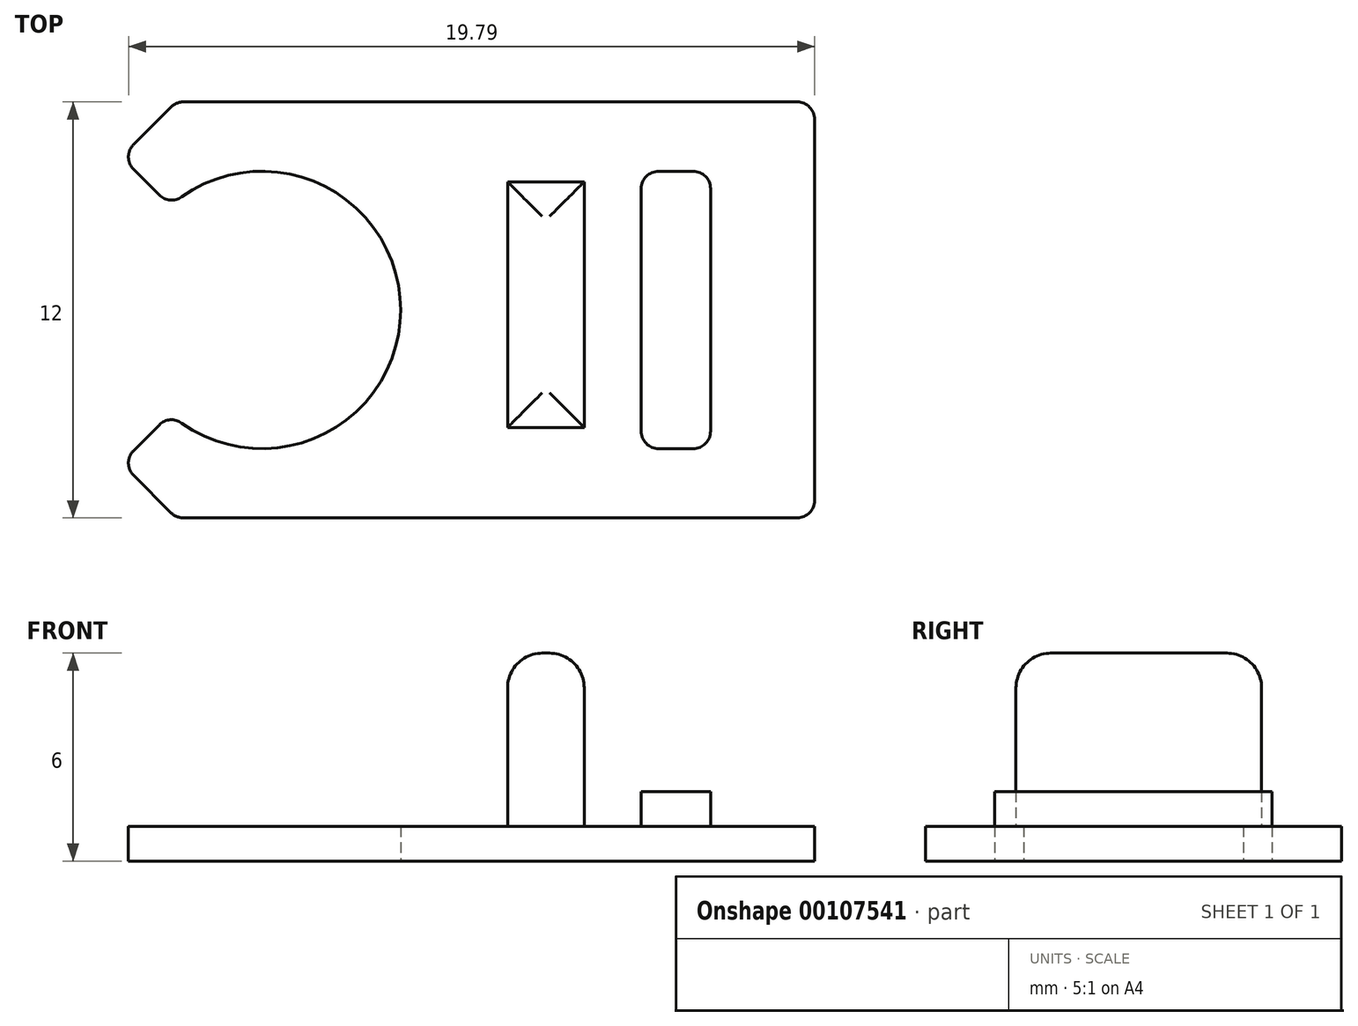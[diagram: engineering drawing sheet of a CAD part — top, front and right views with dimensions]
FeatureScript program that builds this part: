
annotation { "Feature Type Name" : "Feature", "Feature Type Description" : "" }
export const myFeature = defineFeature(function(context is Context, id is Id, definition is map)
    precondition{}
    {
        {
            var Q0;
            Q0=qCreatedBy(makeId("Top.planeOp"),FACE);
            var sketch = newSketch(context, id + "F0", { "sketchPlane" : qUnion([Q0])});
            skArc(sketch, "E0", {"start": v(-2.65, -3) * mm, "mid": v(4, 0) * mm, "end": v(-2.65, 3) * mm});
            skLineSegment(sketch, "E1", {"start": v(-2.65, 3) * mm, "end": v(-4.06, 4.41) * mm});
            skLineSegment(sketch, "E2", {"start": v(-4.06, 4.41) * mm, "end": v(-2.47, 6) * mm});
            skLineSegment(sketch, "E3", {"start": v(-2.47, 6) * mm, "end": v(15.94, 6) * mm});
            skLineSegment(sketch, "E4", {"start": v(15.94, 6) * mm, "end": v(15.94, -6) * mm});
            skLineSegment(sketch, "E5", {"start": v(15.94, -6) * mm, "end": v(-2.47, -6) * mm});
            skLineSegment(sketch, "E6", {"start": v(-2.47, -6) * mm, "end": v(-4.06, -4.41) * mm});
            skLineSegment(sketch, "E7", {"start": v(-4.06, -4.41) * mm, "end": v(-2.65, -3) * mm});
            skLineSegment(sketch, "E8", {"start": v(-2.65, 3) * mm, "end": v(-2.65, -3) * mm, "construction": true});
            skLineSegment(sketch, "E9", {"start": v(0, 0) * mm, "end": v(-2.65, 0) * mm, "construction": true});
            skSolve(sketch);
        }
        {
            var Q0;
            Q0 = qSketchRegion(id + "F0", true);
            extrude(context, id + "F1", {"entities" : qUnion([Q0]), "depth" : 1 * mm});
        }
        {
            var Q0;
            Q0=makeQuery(id+"F1.opExtrude","CAP_FACE",FACE,{"disambiguationData":[OSD([sQuery(id+"F0.wireOp",EDGE,"E0"),sQuery(id+"F0.wireOp",EDGE,"E1"),sQuery(id+"F0.wireOp",EDGE,"E2"),sQuery(id+"F0.wireOp",EDGE,"E3"),sQuery(id+"F0.wireOp",EDGE,"E4"),sQuery(id+"F0.wireOp",EDGE,"E5"),sQuery(id+"F0.wireOp",EDGE,"E6"),sQuery(id+"F0.wireOp",EDGE,"E7")])],"isStart":false});
            var sketch = newSketch(context, id + "F2", { "sketchPlane" : qUnion([Q0])});
            skLineSegment(sketch, "E10.bottom", {"start": v(10.94, 4) * mm, "end": v(12.94, 4) * mm});
            skLineSegment(sketch, "E10.top", {"start": v(10.94, -4) * mm, "end": v(12.94, -4) * mm});
            skLineSegment(sketch, "E10.left", {"start": v(10.94, 4) * mm, "end": v(10.94, -4) * mm});
            skLineSegment(sketch, "E10.right", {"start": v(12.94, 4) * mm, "end": v(12.94, -4) * mm});
            skLineSegment(sketch, "E11", {"start": v(0, 0) * mm, "end": v(10.94, 0) * mm, "construction": true});
            skSolve(sketch);
        }
        {
            var Q0;
            Q0 = qSketchRegion(id + "F2", true);
            extrude(context, id + "F3", {"entities" : qUnion([Q0]), "operationType" : NewBodyOperationType.ADD, "depth" : 1 * mm});
        }
        {
            var Q0;
            Q0=makeQuery(id+"FxF9EGAjR56P1E0_1.boolean.opBoolean","MERGE",EDGE,{"derivedFrom":[makeQuery(id+"F1.opExtrude","SWEPT_EDGE",EDGE,{"disambiguationData":[OSD([sQuery(id+"F0.wireOp",EDGE,"E4"),sQuery(id+"F0.wireOp",EDGE,"E5")])]}),makeQuery(id+"FxF9EGAjR56P1E0_1.opExtrude","SWEPT_EDGE",EDGE,{"disambiguationData":[OSD([sQuery(id+"Fv8JB0qovILL5Yh_1.wireOp",EDGE,"e5Tw2kPN-vUrT-GTGC-gzv6-bLBOiwCRqEJe.top"),sQuery(id+"Fv8JB0qovILL5Yh_1.wireOp",EDGE,"e5Tw2kPN-vUrT-GTGC-gzv6-bLBOiwCRqEJe.right")])]})]});
            var Q1;
            Q1=makeQuery(id+"FxF9EGAjR56P1E0_1.boolean.opBoolean","MERGE",EDGE,{"derivedFrom":[makeQuery(id+"F1.opExtrude","SWEPT_EDGE",EDGE,{"disambiguationData":[OSD([sQuery(id+"F0.wireOp",EDGE,"E3"),sQuery(id+"F0.wireOp",EDGE,"E4")])]}),makeQuery(id+"FxF9EGAjR56P1E0_1.opExtrude","SWEPT_EDGE",EDGE,{"disambiguationData":[OSD([sQuery(id+"Fv8JB0qovILL5Yh_1.wireOp",EDGE,"e5Tw2kPN-vUrT-GTGC-gzv6-bLBOiwCRqEJe.bottom"),sQuery(id+"Fv8JB0qovILL5Yh_1.wireOp",EDGE,"e5Tw2kPN-vUrT-GTGC-gzv6-bLBOiwCRqEJe.right")])]})]});
            var Q2;
            Q2=makeQuery(id+"F1.opExtrude","SWEPT_EDGE",EDGE,{"disambiguationData":[OSD([sQuery(id+"F0.wireOp",EDGE,"E0"),sQuery(id+"F0.wireOp",EDGE,"E7")])]});
            var Q3;
            Q3=makeQuery(id+"F1.opExtrude","SWEPT_EDGE",EDGE,{"disambiguationData":[OSD([sQuery(id+"F0.wireOp",EDGE,"E0"),sQuery(id+"F0.wireOp",EDGE,"E1")])]});
            var Q4;
            Q4=makeQuery(id+"F1.opExtrude","SWEPT_EDGE",EDGE,{"disambiguationData":[OSD([sQuery(id+"F0.wireOp",EDGE,"E6"),sQuery(id+"F0.wireOp",EDGE,"E7")])]});
            var Q5;
            Q5=makeQuery(id+"F1.opExtrude","SWEPT_EDGE",EDGE,{"disambiguationData":[OSD([sQuery(id+"F0.wireOp",EDGE,"E5"),sQuery(id+"F0.wireOp",EDGE,"E6")])]});
            var Q6;
            Q6=makeQuery(id+"F1.opExtrude","SWEPT_EDGE",EDGE,{"disambiguationData":[OSD([sQuery(id+"F0.wireOp",EDGE,"E1"),sQuery(id+"F0.wireOp",EDGE,"E2")])]});
            var Q7;
            Q7=makeQuery(id+"F1.opExtrude","SWEPT_EDGE",EDGE,{"disambiguationData":[OSD([sQuery(id+"F0.wireOp",EDGE,"E2"),sQuery(id+"F0.wireOp",EDGE,"E3")])]});
            var Q8;
            Q8=makeQuery(id+"F3.opExtrude","SWEPT_EDGE",EDGE,{"disambiguationData":[OSD([sQuery(id+"F2.wireOp",EDGE,"E10.top"),sQuery(id+"F2.wireOp",EDGE,"E10.left")])]});
            var Q9;
            Q9=makeQuery(id+"F3.opExtrude","SWEPT_EDGE",EDGE,{"disambiguationData":[OSD([sQuery(id+"F2.wireOp",EDGE,"E10.top"),sQuery(id+"F2.wireOp",EDGE,"E10.right")])]});
            var Q10;
            Q10=makeQuery(id+"F3.opExtrude","SWEPT_EDGE",EDGE,{"disambiguationData":[OSD([sQuery(id+"F2.wireOp",EDGE,"E10.bottom"),sQuery(id+"F2.wireOp",EDGE,"E10.left")])]});
            var Q11;
            Q11=makeQuery(id+"F3.opExtrude","SWEPT_EDGE",EDGE,{"disambiguationData":[OSD([sQuery(id+"F2.wireOp",EDGE,"E10.bottom"),sQuery(id+"F2.wireOp",EDGE,"E10.right")])]});
            fillet(context, id + "F4", {"entities" : qUnion([Q0, Q1, Q2, Q3, Q4, Q5, Q6, Q7, Q8, Q9, Q10, Q11]), "radius" : 0.5 * mm, "tangentPropagation" : true, "allowEdgeOverflow" : false});
        }
        {
            var Q0;
            Q0=makeQuery(id+"F1.opExtrude","CAP_FACE",FACE,{"disambiguationData":[OSD([sQuery(id+"F0.wireOp",EDGE,"E0"),sQuery(id+"F0.wireOp",EDGE,"E1"),sQuery(id+"F0.wireOp",EDGE,"E2"),sQuery(id+"F0.wireOp",EDGE,"E3"),sQuery(id+"F0.wireOp",EDGE,"E4"),sQuery(id+"F0.wireOp",EDGE,"E5"),sQuery(id+"F0.wireOp",EDGE,"E6"),sQuery(id+"F0.wireOp",EDGE,"E7")])],"isStart":false});
            var sketch = newSketch(context, id + "F5", { "sketchPlane" : qUnion([Q0])});
            skLineSegment(sketch, "E12.bottom", {"start": v(7.08, 3.7) * mm, "end": v(9.3, 3.7) * mm});
            skLineSegment(sketch, "E12.top", {"start": v(7.08, -3.39) * mm, "end": v(9.3, -3.39) * mm});
            skLineSegment(sketch, "E12.left", {"start": v(7.08, 3.7) * mm, "end": v(7.08, -3.39) * mm});
            skLineSegment(sketch, "E12.right", {"start": v(9.3, 3.7) * mm, "end": v(9.3, -3.39) * mm});
            skSolve(sketch);
        }
        {
            var Q0;
            Q0=makeQuery(id+"F5.imprint","IMPRINT",FACE,{"disambiguationData":[TD([[makeQuery(id+"F5.imprint","IMPRINT",EDGE,{"derivedFrom":sQuery(id+"F5.wireOp",EDGE,"E12.bottom")}),-1.0]])]});
            extrude(context, id + "F6", {"entities" : qUnion([Q0]), "operationType" : NewBodyOperationType.ADD, "depth" : 5 * mm});
        }
        {
            var Q0;
            Q0=makeQuery(id+"F6.opExtrude","CAP_FACE",FACE,{"disambiguationData":[OSD([sQuery(id+"F5.wireOp",EDGE,"E12.bottom"),sQuery(id+"F5.wireOp",EDGE,"E12.top"),sQuery(id+"F5.wireOp",EDGE,"E12.left"),sQuery(id+"F5.wireOp",EDGE,"E12.right")])],"isStart":false});
            fillet(context, id + "F7", {"entities" : qUnion([Q0]), "radius" : 1 * mm, "tangentPropagation" : true, "allowEdgeOverflow" : false});
        }
    });
